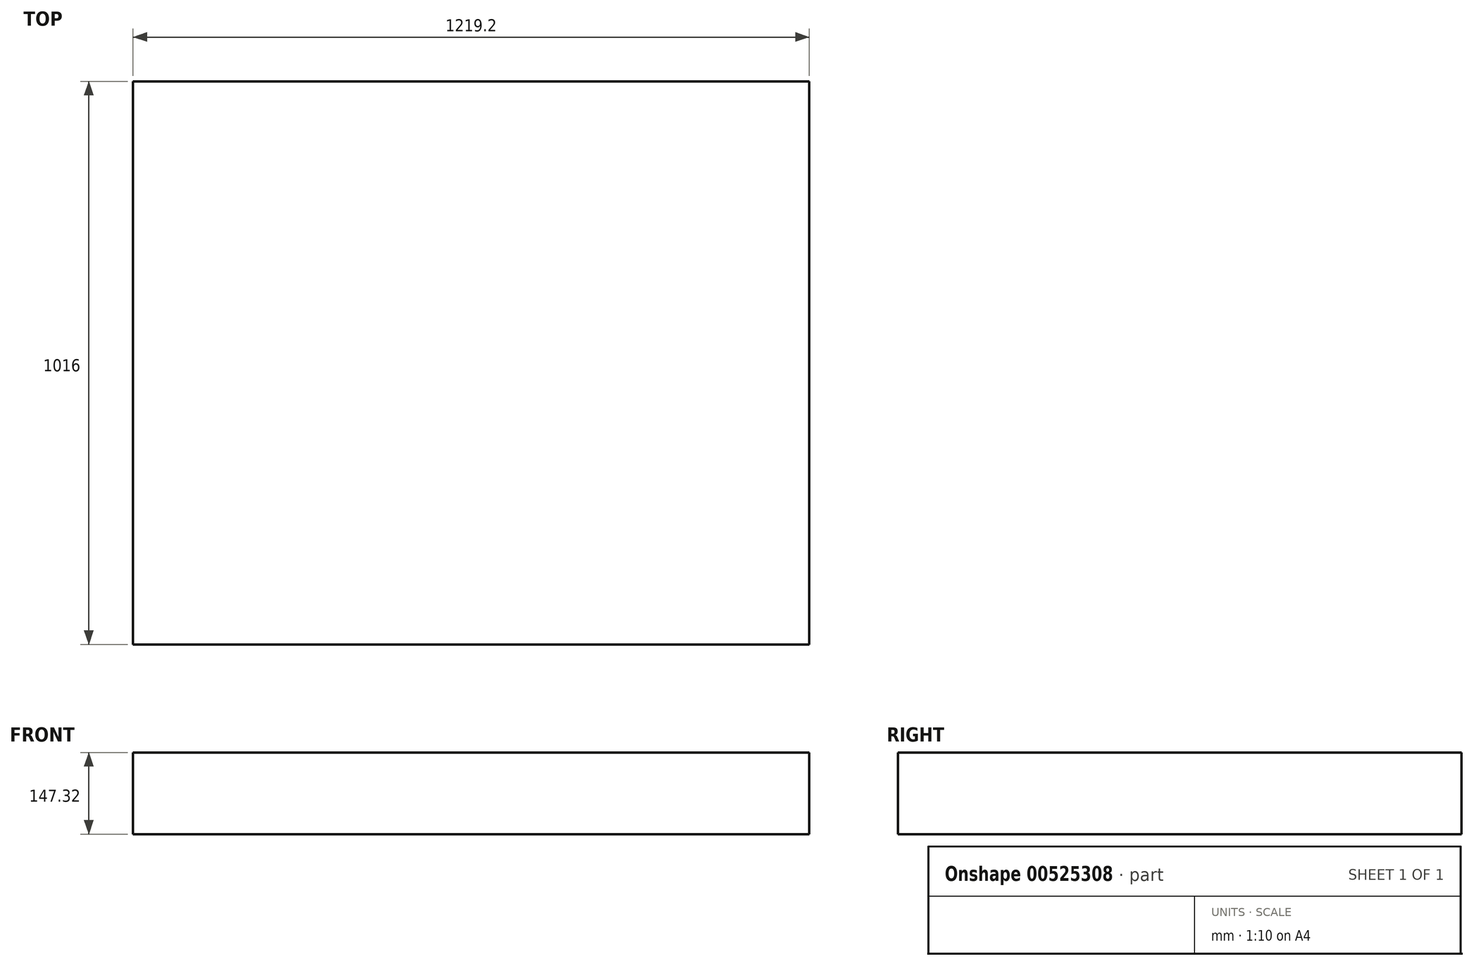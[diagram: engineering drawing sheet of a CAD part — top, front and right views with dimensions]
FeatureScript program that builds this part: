
annotation { "Feature Type Name" : "Feature", "Feature Type Description" : "" }
export const myFeature = defineFeature(function(context is Context, id is Id, definition is map)
    precondition{}
    {
        {
            var Q0;
            Q0=qCreatedBy(makeId("Top.planeOp"),FACE);
            var sketch = newSketch(context, id + "F0", { "sketchPlane" : qUnion([Q0])});
            skLineSegment(sketch, "E0.bottom", {"start": v(609.6, 508) * mm, "end": v(-609.6, 508) * mm});
            skLineSegment(sketch, "E0.top", {"start": v(609.6, -508) * mm, "end": v(-609.6, -508) * mm});
            skLineSegment(sketch, "E0.left", {"start": v(609.6, 508) * mm, "end": v(609.6, -508) * mm});
            skLineSegment(sketch, "E0.right", {"start": v(-609.6, 508) * mm, "end": v(-609.6, -508) * mm});
            skPoint(sketch, "E0.middle", {"position": v(0, 0) * mm});
            skSolve(sketch);
        }
        {
            var Q0;
            Q0=makeQuery(id+"F0.imprint","IMPRINT",FACE,{"disambiguationData":[TD([[makeQuery(id+"F0.imprint","IMPRINT",EDGE,{"derivedFrom":sQuery(id+"F0.wireOp",EDGE,"E0.bottom")}),1.0]])]});
            extrude(context, id + "F1", {"entities" : qUnion([Q0]), "depth" : 147.32 * mm, "offsetDistance" : 25.4 * mm});
        }
    });
